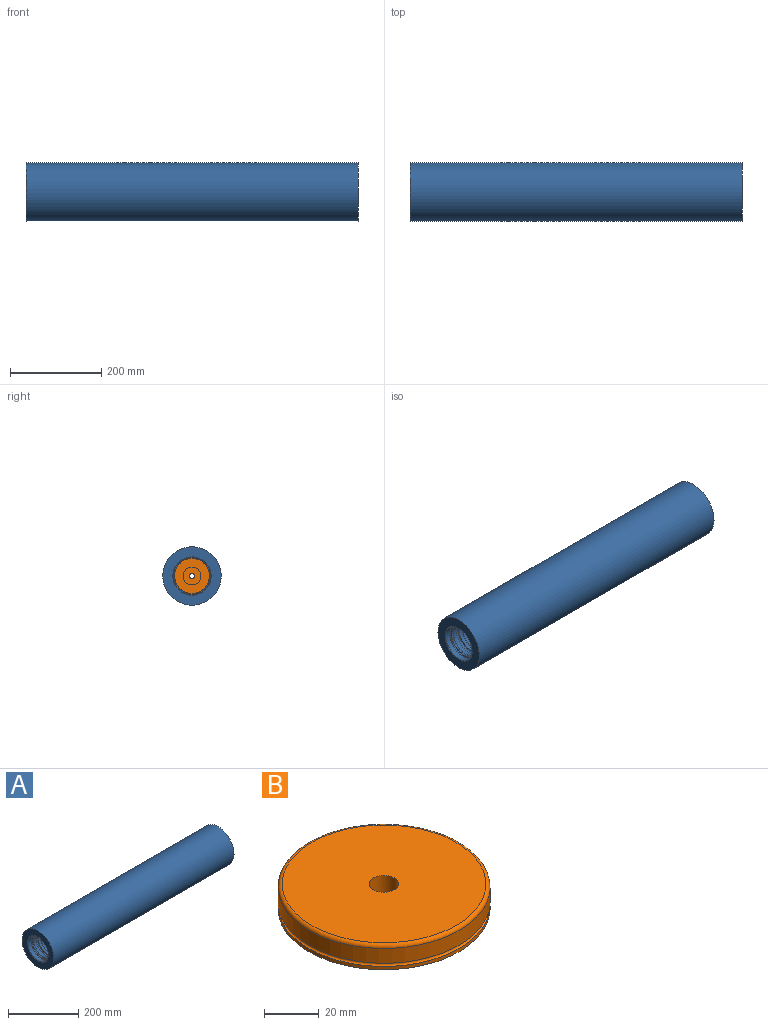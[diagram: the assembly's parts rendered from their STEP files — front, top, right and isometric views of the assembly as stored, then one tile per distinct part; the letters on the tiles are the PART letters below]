
ASSEMBLY  parts=2 mates=1
PART A: 59 faces, bbox 726.4x127.8x127.8 mm
  f0: cylinder r=38.82mm len=77.65mm, axis (-1,0,0), area 2150mm2, adj f11,f43
  f1: cylinder r=38.82mm len=77.65mm, axis (-1,0,0), area 1858.8mm2, adj f9,f39
  f2: cylinder r=38.82mm len=77.65mm, axis (-1,0,0), area 1530.4mm2, adj f12,f17
  f3: cylinder r=38.82mm len=77.65mm, axis (-1,0,0), area 2323.5mm2, adj f14,f42
  f4: cylinder r=28.45mm len=536.58mm, axis (-1,0,0), area 95909.6mm2, adj f6,f8
  f5: cylinder r=63.88mm len=726.44mm, axis (-1,0,0), area 291575.7mm2, adj f6,f7
  f6: plane 127.76x127.76mm, normal (1,0,0), area 10277.7mm2, adj f4,f5
  f7: plane 127.76x127.76mm, normal (-1,0,0), area 7296.1mm2, adj f5,f49
  f8: plane 74.6x74.6mm, normal (-1,0,0), area 1828.4mm2, adj f4,f42
  f9: plane 82.12x82.12mm, normal (-1,0,0), area 560.9mm2, adj f1,f50
  f10: cylinder r=41.82mm len=83.64mm, axis (-1,0,0), area 2022.3mm2, adj f11,f50
  f11: plane 83.64x83.64mm, normal (1,0,0), area 759.4mm2, adj f0,f10
  f12: plane 82.7x82.7mm, normal (1,0,0), area 636.6mm2, adj f2,f57
  f13: cylinder r=42.11mm len=84.23mm, axis (-1,0,0), area 1834.8mm2, adj f57,f58
  f14: plane 82.7x82.7mm, normal (-1,0,0), area 636.6mm2, adj f3,f58
  f15: cone r=39.59mm half-angle=15deg, axis (1,0,0), area 725.2mm2, adj f16,f22
  f16: cylinder r=39.59mm len=79.17mm, axis (-1,0,0), area 1428.3mm2, adj f15,f17
  f17: cone r=38.82mm half-angle=15deg, axis (-1,0,0), area 725.2mm2, adj f2,f16
  f18: plane 82.12x82.12mm, normal (1,0,0), area 560.9mm2, adj f19,f55
  f19: cylinder r=38.82mm len=77.65mm, axis (-1,0,0), area 1840.2mm2, adj f18,f25
  f20: cylinder r=41.82mm len=83.64mm, axis (-1,0,0), area 1822.1mm2, adj f55,f56
  f21: plane 82.12x82.12mm, normal (-1,0,0), area 560.9mm2, adj f22,f56
  f22: cylinder r=38.82mm len=77.65mm, axis (-1,0,0), area 1858.8mm2, adj f15,f21
  f23: cone r=39.59mm half-angle=15deg, axis (1,0,0), area 725.2mm2, adj f24,f30
  f24: cylinder r=39.59mm len=79.17mm, axis (-1,0,0), area 1428.3mm2, adj f23,f25
  f25: cone r=38.82mm half-angle=15deg, axis (-1,0,0), area 725.2mm2, adj f19,f24
  f26: plane 82.12x82.12mm, normal (1,0,0), area 560.9mm2, adj f27,f53
  f27: cylinder r=38.82mm len=77.65mm, axis (-1,0,0), area 1840.2mm2, adj f26,f33
  f28: cylinder r=41.82mm len=83.64mm, axis (-1,0,0), area 1822.1mm2, adj f53,f54
  f29: plane 82.12x82.12mm, normal (-1,0,0), area 560.9mm2, adj f30,f54
  f30: cylinder r=38.82mm len=77.65mm, axis (-1,0,0), area 1858.8mm2, adj f23,f29
  f31: cone r=39.59mm half-angle=15deg, axis (1,0,0), area 725.2mm2, adj f32,f38
  f32: cylinder r=39.59mm len=79.17mm, axis (-1,0,0), area 1428.3mm2, adj f31,f33
  f33: cone r=38.82mm half-angle=15deg, axis (-1,0,0), area 725.2mm2, adj f27,f32
  f34: plane 82.12x82.12mm, normal (1,0,0), area 560.9mm2, adj f35,f51
  f35: cylinder r=38.82mm len=77.65mm, axis (-1,0,0), area 1840.2mm2, adj f34,f41
  f36: cylinder r=41.82mm len=83.64mm, axis (-1,0,0), area 1822.1mm2, adj f51,f52
  f37: plane 82.12x82.12mm, normal (-1,0,0), area 560.9mm2, adj f38,f52
  f38: cylinder r=38.82mm len=77.65mm, axis (-1,0,0), area 1858.8mm2, adj f31,f37
  f39: cone r=39.59mm half-angle=15deg, axis (1,0,0), area 725.2mm2, adj f1,f40
  f40: cylinder r=39.59mm len=79.17mm, axis (-1,0,0), area 1428.3mm2, adj f39,f41
  f41: cone r=38.82mm half-angle=15deg, axis (-1,0,0), area 725.2mm2, adj f35,f40
  f42: torus R=37.3mm, axis (-1,0,0), area 575.6mm2, adj f3,f8
  f43: cone r=38.82mm half-angle=30deg, axis (-1,0,0), area 268.3mm2, adj f0,f44
  f44: cylinder r=39.37mm len=78.74mm, axis (-1,0,0), area 959.8mm2, adj f43,f45
  f45: plane 84.12x84.12mm, normal (-1,0,0), area 688.8mm2, adj f44,f46
  f46: cylinder r=42.06mm len=84.12mm, axis (-1,0,0), area 537mm2, adj f45,f47
  f47: cone r=42.06mm half-angle=30deg, axis (1,0,0), area 597.3mm2, adj f46,f48
  f48: cylinder r=40.92mm len=81.83mm, axis (-1,0,0), area 3277.3mm2, adj f47,f49
  f49: cone r=40.92mm half-angle=45deg, axis (-1,0,0), area 374mm2, adj f7,f48
  f50: torus R=41.06mm, axis (-1,0,0), area 312.4mm2, adj f9,f10
  f51: torus R=41.06mm, axis (1,0,0), area 312.4mm2, adj f34,f36
  f52: torus R=41.06mm, axis (-1,0,0), area 312.4mm2, adj f36,f37
  f53: torus R=41.06mm, axis (1,0,0), area 312.4mm2, adj f26,f28
  f54: torus R=41.06mm, axis (-1,0,0), area 312.4mm2, adj f28,f29
  f55: torus R=41.06mm, axis (1,0,0), area 312.4mm2, adj f18,f20
  f56: torus R=41.06mm, axis (-1,0,0), area 312.4mm2, adj f20,f21
  f57: torus R=41.35mm, axis (1,0,0), area 314.6mm2, adj f12,f13
  f58: torus R=41.35mm, axis (-1,0,0), area 314.6mm2, adj f13,f14
PART B: 9 faces, bbox 85.2x85.2x11 mm
  f0: torus R=38.84mm, axis (0,0,-1), area 558mm2, adj f1,f7
  f1: cylinder r=38.84mm len=77.67mm, axis (0,0,-1), area 355.6mm2, adj f0,f2
  f2: plane 77.67x77.67mm, normal (0,0,-1), area 3529.8mm2, adj f1,f3
  f3: cylinder r=19.61mm len=39.23mm, axis (0,0,-1), area 408mm2, adj f2,f4
  f4: plane 39.23x39.23mm, normal (0,0,-1), area 1118.4mm2, adj f3,f8
  f5: plane 74.63x74.63mm, normal (0,0,1), area 4283.6mm2, adj f6,f8
  f6: torus R=37.31mm, axis (0,0,-1), area 575.8mm2, adj f5,f7
  f7: cylinder r=38.84mm len=77.67mm, axis (0,0,-1), area 1609.2mm2, adj f0,f6
  f8: cylinder r=5.36mm len=10.72mm, axis (0,0,-1), area 260.5mm2, adj f4,f5
PLACE A rot(axis=(-1,0,0),0deg) t=(289.8,40.78,-94.64)mm
PLACE B rot(axis=(0,1,0),90deg) t=(105.71,40.78,-94.64)mm
MATE cylindrical B.f0 <-> A.f42  axis (-1,0,0) through (111.94,40.78,-94.64)mm
